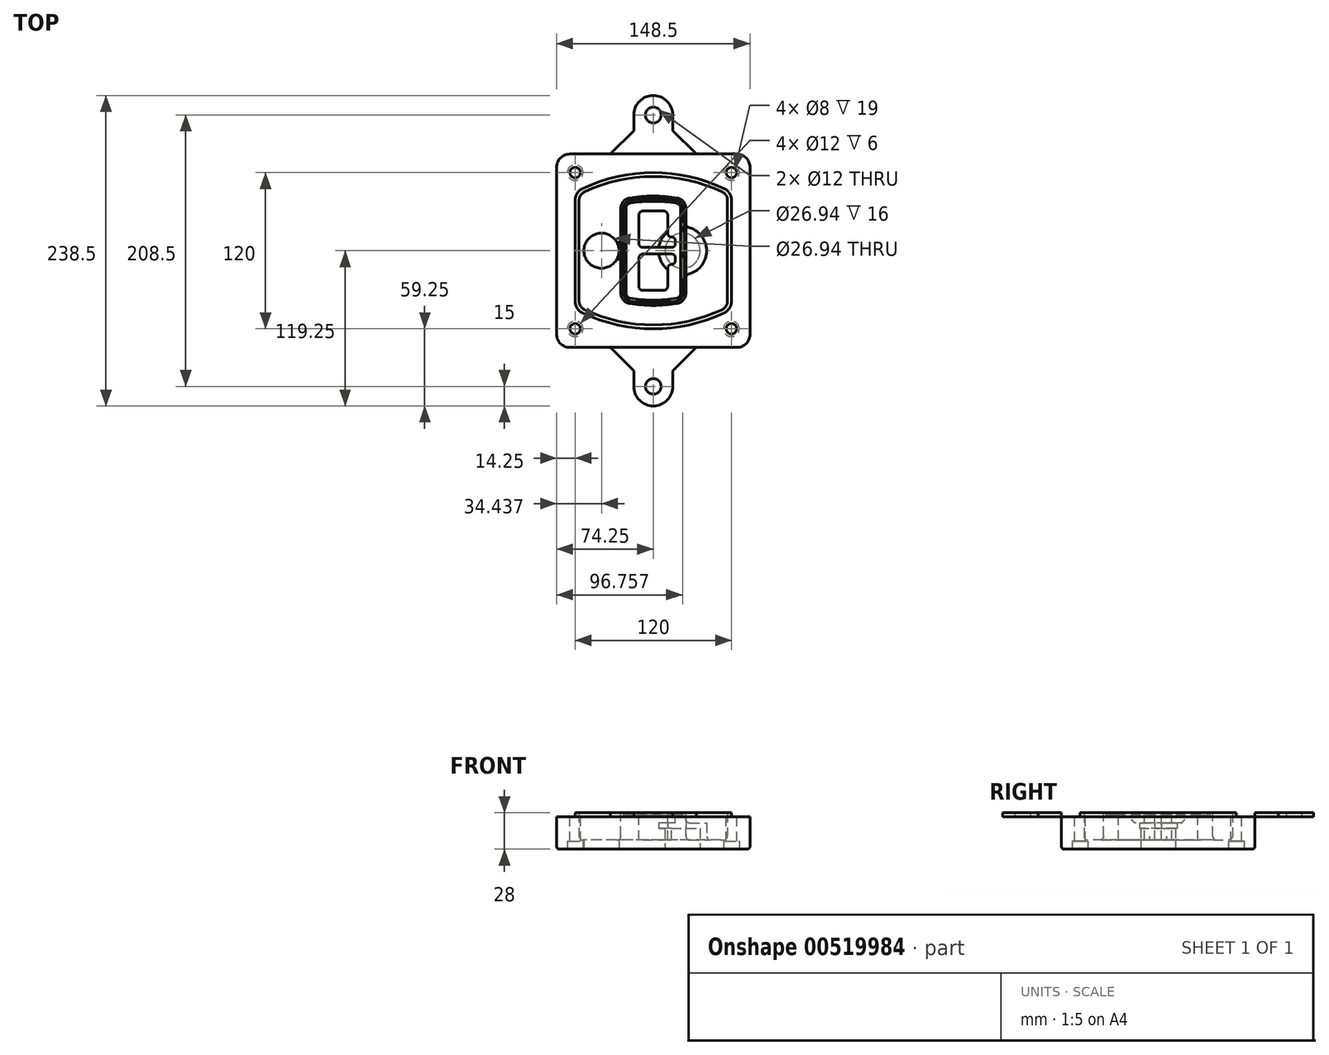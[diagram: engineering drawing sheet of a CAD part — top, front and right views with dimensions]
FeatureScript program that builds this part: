
annotation { "Feature Type Name" : "Feature", "Feature Type Description" : "" }
export const myFeature = defineFeature(function(context is Context, id is Id, definition is map)
    precondition{}
    {
        {
            var Q0;
            Q0=qCreatedBy(makeId("Top.planeOp"),FACE);
            var sketch = newSketch(context, id + "F0", { "sketchPlane" : qUnion([Q0])});
            skPoint(sketch, "E0.rect.middle", {"position": v(0, 0) * mm});
            skLineSegment(sketch, "E1.bottom", {"start": v(-64.25, -74.25) * mm, "end": v(64.25, -74.25) * mm});
            skLineSegment(sketch, "E1.top", {"start": v(-64.25, 74.25) * mm, "end": v(64.25, 74.25) * mm});
            skLineSegment(sketch, "E1.left", {"start": v(-74.25, -64.25) * mm, "end": v(-74.25, 64.25) * mm});
            skLineSegment(sketch, "E1.right", {"start": v(74.25, -64.25) * mm, "end": v(74.25, 64.25) * mm});
            skLineSegment(sketch, "E2", {"start": v(-74.25, 74.25) * mm, "end": v(74.25, -74.25) * mm, "construction": true});
            skLineSegment(sketch, "E3", {"start": v(74.25, 74.25) * mm, "end": v(-74.25, -74.25) * mm, "construction": true});
            skCircle(sketch, "E4", {"center": v(-60, 60) * mm, "radius": 4 * mm});
            skCircle(sketch, "E5", {"center": v(60, 60) * mm, "radius": 4 * mm});
            skCircle(sketch, "E6", {"center": v(60, -60) * mm, "radius": 4 * mm});
            skCircle(sketch, "E7", {"center": v(-60, -60) * mm, "radius": 4 * mm});
            skLineSegment(sketch, "E8", {"start": v(-60, 60) * mm, "end": v(60, 60) * mm, "construction": true});
            skLineSegment(sketch, "E9", {"start": v(60, 60) * mm, "end": v(60, -60) * mm, "construction": true});
            skLineSegment(sketch, "E10", {"start": v(60, -60) * mm, "end": v(-60, -60) * mm, "construction": true});
            skLineSegment(sketch, "E11", {"start": v(-60, -60) * mm, "end": v(-60, 60) * mm, "construction": true});
            skLineSegment(sketch, "E12", {"start": v(-60, 38.83) * mm, "end": v(-60, -38.83) * mm});
            skLineSegment(sketch, "E13", {"start": v(60, 38.83) * mm, "end": v(60, -38.83) * mm});
            skArc(sketch, "E14", {"start": v(54.26, 47.88) * mm, "mid": v(0, 60) * mm, "end": v(-54.26, 47.88) * mm});
            skArc(sketch, "E15", {"start": v(-54.26, -47.88) * mm, "mid": v(0, -60) * mm, "end": v(54.26, -47.88) * mm});
            skLineSegment(sketch, "E16", {"start": v(-60, 0) * mm, "end": v(60, 0) * mm, "construction": true});
            skPoint(sketch, "E17.visualSharp", {"position": v(-60, -45) * mm});
            skArc(sketch, "E17.filletArc", {"start": v(-60, -38.83) * mm, "mid": v(-58.44, -44.2) * mm, "end": v(-54.26, -47.88) * mm});
            skPoint(sketch, "E18.visualSharp", {"position": v(-60, 45) * mm});
            skArc(sketch, "E18.filletArc", {"start": v(-54.26, 47.88) * mm, "mid": v(-58.44, 44.2) * mm, "end": v(-60, 38.83) * mm});
            skPoint(sketch, "E19.visualSharp", {"position": v(60, 45) * mm});
            skArc(sketch, "E19.filletArc", {"start": v(60, 38.83) * mm, "mid": v(58.44, 44.2) * mm, "end": v(54.26, 47.88) * mm});
            skPoint(sketch, "E20.visualSharp", {"position": v(60, -45) * mm});
            skArc(sketch, "E20.filletArc", {"start": v(54.26, -47.88) * mm, "mid": v(58.44, -44.2) * mm, "end": v(60, -38.83) * mm});
            skPoint(sketch, "E21.visualSharp", {"position": v(-74.25, 74.25) * mm});
            skArc(sketch, "E21.filletArc", {"start": v(-64.25, 74.25) * mm, "mid": v(-71.32, 71.32) * mm, "end": v(-74.25, 64.25) * mm});
            skPoint(sketch, "E22.visualSharp", {"position": v(74.25, 74.25) * mm});
            skArc(sketch, "E22.filletArc", {"start": v(74.25, 64.25) * mm, "mid": v(71.32, 71.32) * mm, "end": v(64.25, 74.25) * mm});
            skPoint(sketch, "E23.visualSharp", {"position": v(74.25, -74.25) * mm});
            skArc(sketch, "E23.filletArc", {"start": v(64.25, -74.25) * mm, "mid": v(71.32, -71.32) * mm, "end": v(74.25, -64.25) * mm});
            skPoint(sketch, "E24.visualSharp", {"position": v(-74.25, -74.25) * mm});
            skArc(sketch, "E24.filletArc", {"start": v(-74.25, -64.25) * mm, "mid": v(-71.32, -71.32) * mm, "end": v(-64.25, -74.25) * mm});
            skArc(sketch, "E25.0", {"start": v(57, 38.83) * mm, "mid": v(55.9, 42.58) * mm, "end": v(52.98, 45.17) * mm});
            skLineSegment(sketch, "E25.1", {"start": v(57, 38.83) * mm, "end": v(57, -38.83) * mm});
            skArc(sketch, "E25.2", {"start": v(52.98, -45.17) * mm, "mid": v(55.9, -42.58) * mm, "end": v(57, -38.83) * mm});
            skArc(sketch, "E25.3", {"start": v(-52.98, -45.17) * mm, "mid": v(0, -57) * mm, "end": v(52.98, -45.17) * mm});
            skArc(sketch, "E25.4", {"start": v(-57, -38.83) * mm, "mid": v(-55.9, -42.58) * mm, "end": v(-52.98, -45.17) * mm});
            skArc(sketch, "E25.5", {"start": v(52.98, 45.17) * mm, "mid": v(0, 57) * mm, "end": v(-52.98, 45.17) * mm});
            skLineSegment(sketch, "E25.6", {"start": v(-57, 38.83) * mm, "end": v(-57, -38.83) * mm});
            skArc(sketch, "E25.7", {"start": v(-52.98, 45.17) * mm, "mid": v(-55.9, 42.58) * mm, "end": v(-57, 38.83) * mm});
            skArc(sketch, "E26.0", {"start": v(-55.96, 51.5) * mm, "mid": v(-61.82, 46.33) * mm, "end": v(-64, 38.83) * mm});
            skArc(sketch, "E26.1", {"start": v(55.96, 51.5) * mm, "mid": v(0, 64) * mm, "end": v(-55.96, 51.5) * mm});
            skArc(sketch, "E26.2", {"start": v(64, 38.83) * mm, "mid": v(61.82, 46.33) * mm, "end": v(55.96, 51.5) * mm});
            skLineSegment(sketch, "E26.3", {"start": v(64, 38.83) * mm, "end": v(64, -38.83) * mm});
            skArc(sketch, "E26.4", {"start": v(55.96, -51.5) * mm, "mid": v(61.82, -46.33) * mm, "end": v(64, -38.83) * mm});
            skLineSegment(sketch, "E26.5", {"start": v(-64, 38.83) * mm, "end": v(-64, -38.83) * mm});
            skArc(sketch, "E26.6", {"start": v(-55.96, -51.5) * mm, "mid": v(0, -64) * mm, "end": v(55.96, -51.5) * mm});
            skArc(sketch, "E26.7", {"start": v(-64, -38.83) * mm, "mid": v(-61.82, -46.33) * mm, "end": v(-55.96, -51.5) * mm});
            skSolve(sketch);
        }
        {
            var Q0;
            Q0=makeQuery(id+"F0.imprint","IMPRINT",FACE,{"disambiguationData":[TD([[makeQuery(id+"F0.imprint","IMPRINT",EDGE,{"derivedFrom":sQuery(id+"F0.wireOp",EDGE,"E1.bottom")}),1.0]])]});
            var Q1;
            Q1=makeQuery(id+"F0.imprint","IMPRINT",FACE,{"disambiguationData":[TD([[makeQuery(id+"F0.imprint","IMPRINT",EDGE,{"derivedFrom":sQuery(id+"F0.wireOp",EDGE,"E12")}),1.0]])]});
            var Q2;
            Q2=makeQuery(id+"F0.imprint","IMPRINT",FACE,{"disambiguationData":[TD([[makeQuery(id+"F0.imprint","IMPRINT",EDGE,{"derivedFrom":sQuery(id+"F0.wireOp",EDGE,"E25.0")}),1.0]])]});
            var Q3;
            Q3=makeQuery(id+"F0.imprint","IMPRINT",FACE,{"disambiguationData":[TD([[makeQuery(id+"F0.imprint","IMPRINT",EDGE,{"derivedFrom":sQuery(id+"F0.wireOp",EDGE,"E12")}),-1.0]])]});
            extrude(context, id + "F1", {"entities" : qUnion([Q0, Q1, Q2, Q3]), "oppositeDirection" : true, "depth" : 25 * mm});
        }
        {
            var Q0;
            Q0=makeQuery(id+"F0.imprint","IMPRINT",FACE,{"disambiguationData":[TD([[makeQuery(id+"F0.imprint","IMPRINT",EDGE,{"derivedFrom":sQuery(id+"F0.wireOp",EDGE,"E12")}),1.0]])]});
            extrude(context, id + "F2", {"entities" : qUnion([Q0]), "operationType" : NewBodyOperationType.ADD, "depth" : 3 * mm});
        }
        {
            var Q0;
            Q0=makeQuery(id+"F0.imprint","IMPRINT",FACE,{"disambiguationData":[TD([[makeQuery(id+"F0.imprint","IMPRINT",EDGE,{"derivedFrom":sQuery(id+"F0.wireOp",EDGE,"E25.0")}),1.0]])]});
            extrude(context, id + "F3", {"entities" : qUnion([Q0]), "operationType" : NewBodyOperationType.REMOVE, "oppositeDirection" : true, "depth" : 18 * mm});
        }
        {
            var Q0;
            Q0=makeQuery(id+"F2.opExtrude","CAP_FACE",FACE,{"disambiguationData":[OSD([sQuery(id+"F0.wireOp",EDGE,"E12"),sQuery(id+"F0.wireOp",EDGE,"E13"),sQuery(id+"F0.wireOp",EDGE,"E14"),sQuery(id+"F0.wireOp",EDGE,"E15"),sQuery(id+"F0.wireOp",EDGE,"E17.filletArc"),sQuery(id+"F0.wireOp",EDGE,"E18.filletArc"),sQuery(id+"F0.wireOp",EDGE,"E19.filletArc"),sQuery(id+"F0.wireOp",EDGE,"E20.filletArc"),sQuery(id+"F0.wireOp",EDGE,"E25.0"),sQuery(id+"F0.wireOp",EDGE,"E25.1"),sQuery(id+"F0.wireOp",EDGE,"E25.2"),sQuery(id+"F0.wireOp",EDGE,"E25.3"),sQuery(id+"F0.wireOp",EDGE,"E25.4"),sQuery(id+"F0.wireOp",EDGE,"E25.5"),sQuery(id+"F0.wireOp",EDGE,"E25.6"),sQuery(id+"F0.wireOp",EDGE,"E25.7")])],"isStart":false});
            var sketch = newSketch(context, id + "F4", { "sketchPlane" : qUnion([Q0])});
            skArc(sketch, "E27.0", {"start": v(-18.34, -40.45) * mm, "mid": v(0, -42) * mm, "end": v(18.34, -40.45) * mm});
            skArc(sketch, "E28.0", {"start": v(18.34, 40.45) * mm, "mid": v(0, 42) * mm, "end": v(-18.34, 40.45) * mm});
            skLineSegment(sketch, "E29", {"start": v(-25, 32.57) * mm, "end": v(-25, -32.57) * mm});
            skLineSegment(sketch, "E30", {"start": v(25, 32.57) * mm, "end": v(25, -32.57) * mm});
            skLineSegment(sketch, "E31", {"start": v(-25, 39.1) * mm, "end": v(25, 39.1) * mm, "construction": true});
            skLineSegment(sketch, "E32", {"start": v(-25, -39.1) * mm, "end": v(25, -39.1) * mm, "construction": true});
            skPoint(sketch, "E33.visualSharp", {"position": v(-25, 39.1) * mm});
            skArc(sketch, "E33.filletArc", {"start": v(-18.34, 40.45) * mm, "mid": v(-23.11, 37.73) * mm, "end": v(-25, 32.57) * mm});
            skPoint(sketch, "E34.visualSharp", {"position": v(25, 39.1) * mm});
            skArc(sketch, "E34.filletArc", {"start": v(25, 32.57) * mm, "mid": v(23.11, 37.73) * mm, "end": v(18.34, 40.45) * mm});
            skPoint(sketch, "E35.visualSharp", {"position": v(25, -39.1) * mm});
            skArc(sketch, "E35.filletArc", {"start": v(18.34, -40.45) * mm, "mid": v(23.11, -37.73) * mm, "end": v(25, -32.57) * mm});
            skPoint(sketch, "E36.visualSharp", {"position": v(-25, -39.1) * mm});
            skArc(sketch, "E36.filletArc", {"start": v(-25, -32.57) * mm, "mid": v(-23.11, -37.73) * mm, "end": v(-18.34, -40.45) * mm});
            skArc(sketch, "E37.0", {"start": v(52.98, 45.17) * mm, "mid": v(0, 57) * mm, "end": v(-52.98, 45.17) * mm});
            skArc(sketch, "E37.1", {"start": v(-52.98, 45.17) * mm, "mid": v(-55.9, 42.58) * mm, "end": v(-57, 38.83) * mm});
            skLineSegment(sketch, "E37.2", {"start": v(-57, 38.83) * mm, "end": v(-57, -38.83) * mm});
            skArc(sketch, "E37.3", {"start": v(-57, -38.83) * mm, "mid": v(-55.9, -42.58) * mm, "end": v(-52.98, -45.17) * mm});
            skArc(sketch, "E37.4", {"start": v(-52.98, -45.17) * mm, "mid": v(0, -57) * mm, "end": v(52.98, -45.17) * mm});
            skArc(sketch, "E37.5", {"start": v(52.98, -45.17) * mm, "mid": v(55.9, -42.58) * mm, "end": v(57, -38.83) * mm});
            skLineSegment(sketch, "E37.6", {"start": v(57, 38.83) * mm, "end": v(57, -38.83) * mm});
            skArc(sketch, "E37.7", {"start": v(57, 38.83) * mm, "mid": v(55.9, 42.58) * mm, "end": v(52.98, 45.17) * mm});
            skLineSegment(sketch, "E38.0", {"start": v(23, 32.57) * mm, "end": v(23, -32.57) * mm});
            skArc(sketch, "E38.1", {"start": v(18, -38.48) * mm, "mid": v(21.58, -36.44) * mm, "end": v(23, -32.57) * mm});
            skArc(sketch, "E38.2", {"start": v(-18, -38.48) * mm, "mid": v(0, -40) * mm, "end": v(18, -38.48) * mm});
            skArc(sketch, "E38.3", {"start": v(-23, -32.57) * mm, "mid": v(-21.58, -36.44) * mm, "end": v(-18, -38.48) * mm});
            skLineSegment(sketch, "E38.4", {"start": v(-23, 32.57) * mm, "end": v(-23, -32.57) * mm});
            skArc(sketch, "E38.5", {"start": v(23, 32.57) * mm, "mid": v(21.58, 36.44) * mm, "end": v(18, 38.48) * mm});
            skArc(sketch, "E38.6", {"start": v(-18, 38.48) * mm, "mid": v(-21.58, 36.44) * mm, "end": v(-23, 32.57) * mm});
            skArc(sketch, "E38.7", {"start": v(18, 38.48) * mm, "mid": v(0, 40) * mm, "end": v(-18, 38.48) * mm});
            skArc(sketch, "E39.0", {"start": v(21, 32.57) * mm, "mid": v(20.06, 35.15) * mm, "end": v(17.67, 36.5) * mm});
            skLineSegment(sketch, "E39.1", {"start": v(21, 32.57) * mm, "end": v(21, -32.57) * mm});
            skArc(sketch, "E39.2", {"start": v(17.67, -36.5) * mm, "mid": v(20.06, -35.15) * mm, "end": v(21, -32.57) * mm});
            skArc(sketch, "E39.3", {"start": v(-17.67, -36.5) * mm, "mid": v(0, -38) * mm, "end": v(17.67, -36.5) * mm});
            skArc(sketch, "E39.4", {"start": v(-21, -32.57) * mm, "mid": v(-20.06, -35.15) * mm, "end": v(-17.67, -36.5) * mm});
            skArc(sketch, "E39.5", {"start": v(17.67, 36.5) * mm, "mid": v(0, 38) * mm, "end": v(-17.67, 36.5) * mm});
            skLineSegment(sketch, "E39.6", {"start": v(-21, 32.57) * mm, "end": v(-21, -32.57) * mm});
            skArc(sketch, "E39.7", {"start": v(-17.67, 36.5) * mm, "mid": v(-20.06, 35.15) * mm, "end": v(-21, 32.57) * mm});
            skLineSegment(sketch, "E40", {"start": v(-25, 0) * mm, "end": v(25, 0) * mm, "construction": true});
            skLineSegment(sketch, "E41", {"start": v(-11, 5.5) * mm, "end": v(-11, 27.5) * mm});
            skLineSegment(sketch, "E42", {"start": v(-8, 30.5) * mm, "end": v(8, 30.5) * mm});
            skLineSegment(sketch, "E43", {"start": v(11, 27.5) * mm, "end": v(11, 13.5) * mm});
            skLineSegment(sketch, "E44", {"start": v(14, 10.5) * mm, "end": v(14, 10.5) * mm});
            skLineSegment(sketch, "E45", {"start": v(17, 7.5) * mm, "end": v(17, 5.5) * mm});
            skLineSegment(sketch, "E46", {"start": v(14, 2.5) * mm, "end": v(-8, 2.5) * mm});
            skPoint(sketch, "E47.visualSharp", {"position": v(-11, 30.5) * mm});
            skArc(sketch, "E47.filletArc", {"start": v(-8, 30.5) * mm, "mid": v(-10.12, 29.62) * mm, "end": v(-11, 27.5) * mm});
            skPoint(sketch, "E48.visualSharp", {"position": v(11, 30.5) * mm});
            skArc(sketch, "E48.filletArc", {"start": v(11, 27.5) * mm, "mid": v(10.12, 29.62) * mm, "end": v(8, 30.5) * mm});
            skPoint(sketch, "E49.visualSharp", {"position": v(11, 10.5) * mm});
            skArc(sketch, "E49.filletArc", {"start": v(11, 13.5) * mm, "mid": v(11.88, 11.38) * mm, "end": v(14, 10.5) * mm});
            skPoint(sketch, "E50.visualSharp", {"position": v(17, 10.5) * mm});
            skArc(sketch, "E50.filletArc", {"start": v(17, 7.5) * mm, "mid": v(16.12, 9.62) * mm, "end": v(14, 10.5) * mm});
            skPoint(sketch, "E51.visualSharp", {"position": v(17, 2.5) * mm});
            skArc(sketch, "E51.filletArc", {"start": v(14, 2.5) * mm, "mid": v(16.12, 3.38) * mm, "end": v(17, 5.5) * mm});
            skPoint(sketch, "E52.visualSharp", {"position": v(-11, 2.5) * mm});
            skArc(sketch, "E52.filletArc", {"start": v(-11, 5.5) * mm, "mid": v(-10.12, 3.38) * mm, "end": v(-8, 2.5) * mm});
            skLineSegment(sketch, "E53.0.MirrorCS", {"start": v(14, -2.5) * mm, "end": v(-8, -2.5) * mm});
            skArc(sketch, "E54.0.MirrorCS", {"start": v(-11, -5.5) * mm, "mid": v(-10.12, -3.38) * mm, "end": v(-8, -2.5) * mm});
            skLineSegment(sketch, "E55.0.MirrorCS", {"start": v(-11, -5.5) * mm, "end": v(-11, -27.5) * mm});
            skArc(sketch, "E56.0.MirrorCS", {"start": v(-8, -30.5) * mm, "mid": v(-10.12, -29.62) * mm, "end": v(-11, -27.5) * mm});
            skLineSegment(sketch, "E57.0.MirrorCS", {"start": v(-8, -30.5) * mm, "end": v(8, -30.5) * mm});
            skArc(sketch, "E58.0.MirrorCS", {"start": v(11, -27.5) * mm, "mid": v(10.12, -29.62) * mm, "end": v(8, -30.5) * mm});
            skLineSegment(sketch, "E59.0.MirrorCS", {"start": v(11, -27.5) * mm, "end": v(11, -13.5) * mm});
            skArc(sketch, "E60.0.MirrorCS", {"start": v(11, -13.5) * mm, "mid": v(11.88, -11.38) * mm, "end": v(14, -10.5) * mm});
            skArc(sketch, "E61.0.MirrorCS", {"start": v(17, -7.5) * mm, "mid": v(16.12, -9.62) * mm, "end": v(14, -10.5) * mm});
            skLineSegment(sketch, "E62.0.MirrorCS", {"start": v(17, -7.5) * mm, "end": v(17, -5.5) * mm});
            skArc(sketch, "E63.0.MirrorCS", {"start": v(14, -2.5) * mm, "mid": v(16.12, -3.38) * mm, "end": v(17, -5.5) * mm});
            skSolve(sketch);
        }
        {
            var Q0;
            Q0=makeQuery(id+"F4.imprint","IMPRINT",FACE,{"disambiguationData":[TD([[makeQuery(id+"F4.imprint","IMPRINT",EDGE,{"derivedFrom":sQuery(id+"F4.wireOp",EDGE,"E27.0")}),1.0]])]});
            var Q1;
            Q1=makeQuery(id+"F4.imprint","IMPRINT",FACE,{"disambiguationData":[TD([[makeQuery(id+"F4.imprint","IMPRINT",EDGE,{"derivedFrom":sQuery(id+"F4.wireOp",EDGE,"E38.0")}),-1.0]])]});
            var Q2;
            Q2=makeQuery(id+"F4.imprint","IMPRINT",FACE,{"disambiguationData":[TD([[makeQuery(id+"F4.imprint","IMPRINT",EDGE,{"derivedFrom":sQuery(id+"F4.wireOp",EDGE,"E39.0")}),1.0]])]});
            extrude(context, id + "F5", {"entities" : qUnion([Q0, Q1, Q2]), "operationType" : NewBodyOperationType.ADD, "endBound" : BoundingType.UP_TO_NEXT, "oppositeDirection" : true, "depth" : 25 * mm});
        }
        {
            var Q0;
            Q0=makeQuery(id+"F4.imprint","IMPRINT",FACE,{"disambiguationData":[TD([[makeQuery(id+"F4.imprint","IMPRINT",EDGE,{"derivedFrom":sQuery(id+"F4.wireOp",EDGE,"E38.0")}),-1.0]])]});
            extrude(context, id + "F6", {"entities" : qUnion([Q0]), "operationType" : NewBodyOperationType.REMOVE, "oppositeDirection" : true, "depth" : 2 * mm});
        }
        {
            var Q0;
            Q0=makeQuery(id+"F1.opExtrude","CAP_FACE",FACE,{"disambiguationData":[OSD([sQuery(id+"F0.wireOp",EDGE,"E1.bottom"),sQuery(id+"F0.wireOp",EDGE,"E1.top"),sQuery(id+"F0.wireOp",EDGE,"E1.left"),sQuery(id+"F0.wireOp",EDGE,"E1.right"),sQuery(id+"F0.wireOp",EDGE,"E4"),sQuery(id+"F0.wireOp",EDGE,"E5"),sQuery(id+"F0.wireOp",EDGE,"E6"),sQuery(id+"F0.wireOp",EDGE,"E7"),sQuery(id+"F0.wireOp",EDGE,"E21.filletArc"),sQuery(id+"F0.wireOp",EDGE,"E22.filletArc"),sQuery(id+"F0.wireOp",EDGE,"E23.filletArc"),sQuery(id+"F0.wireOp",EDGE,"E24.filletArc")])],"isStart":false});
            var sketch = newSketch(context, id + "F7", { "sketchPlane" : qUnion([Q0])});
            skCircle(sketch, "E64", {"center": v(22.5, 0) * mm, "radius": 13.47 * mm});
            skCircle(sketch, "E65", {"center": v(-39.81, 0) * mm, "radius": 13.47 * mm});
            skLineSegment(sketch, "E66", {"start": v(74.25, 0) * mm, "end": v(-74.25, 0) * mm});
            skCircle(sketch, "E67", {"center": v(22.5, 0) * mm, "radius": 18.47 * mm});
            skCircle(sketch, "E68", {"center": v(60, -60) * mm, "radius": 6 * mm});
            skCircle(sketch, "E69", {"center": v(-60, -60) * mm, "radius": 6 * mm});
            skCircle(sketch, "E70", {"center": v(-60, 60) * mm, "radius": 6 * mm});
            skCircle(sketch, "E71", {"center": v(60, 60) * mm, "radius": 6 * mm});
            skSolve(sketch);
        }
        {
            var Q0;
            {var subQ1=sQuery(id+"F7.wireOp",EDGE,"E66");var subQ4=sQuery(id+"F7.wireOp",EDGE,"E64");var subQ6=makeQuery(id+"F7.imprint","INTERSECT",VERTEX,{"disambiguationData":[OD(0.0)],"derivedFrom":[subQ4,subQ1]});Q0=makeQuery(id+"F7.imprint","IMPRINT",FACE,{"disambiguationData":[TD([[makeQuery(id+"F7.imprint","IMPRINT",EDGE,{"disambiguationData":[TD([[subQ6,-1.0]])],"derivedFrom":subQ4}),-1.0]])]});}
            var Q1;
            {var subQ0=sQuery(id+"F7.wireOp",EDGE,"E66");var subQ1=sQuery(id+"F7.wireOp",EDGE,"E64");var subQ3=makeQuery(id+"F7.imprint","INTERSECT",VERTEX,{"disambiguationData":[OD(0.0)],"derivedFrom":[subQ1,subQ0]});Q1=makeQuery(id+"F7.imprint","IMPRINT",FACE,{"disambiguationData":[TD([[makeQuery(id+"F7.imprint","IMPRINT",EDGE,{"disambiguationData":[TD([[subQ3,-1.0]])],"derivedFrom":subQ1}),1.0]])]});}
            var Q2;
            {var subQ0=sQuery(id+"F7.wireOp",EDGE,"E66");var subQ1=sQuery(id+"F7.wireOp",EDGE,"E64");var subQ3=makeQuery(id+"F7.imprint","INTERSECT",VERTEX,{"disambiguationData":[OD(0.0)],"derivedFrom":[subQ1,subQ0]});Q2=makeQuery(id+"F7.imprint","IMPRINT",FACE,{"disambiguationData":[TD([[makeQuery(id+"F7.imprint","IMPRINT",EDGE,{"disambiguationData":[TD([[subQ3,1.0]])],"derivedFrom":subQ1}),1.0]])]});}
            var Q3;
            {var subQ1=sQuery(id+"F7.wireOp",EDGE,"E66");var subQ4=sQuery(id+"F7.wireOp",EDGE,"E64");var subQ6=makeQuery(id+"F7.imprint","INTERSECT",VERTEX,{"disambiguationData":[OD(0.0)],"derivedFrom":[subQ4,subQ1]});Q3=makeQuery(id+"F7.imprint","IMPRINT",FACE,{"disambiguationData":[TD([[makeQuery(id+"F7.imprint","IMPRINT",EDGE,{"disambiguationData":[TD([[subQ6,1.0]])],"derivedFrom":subQ4}),-1.0]])]});}
            extrude(context, id + "F8", {"entities" : qUnion([Q0, Q1, Q2, Q3]), "operationType" : NewBodyOperationType.ADD, "oppositeDirection" : true, "depth" : 20 * mm});
        }
        {
            var Q0;
            {var subQ0=sQuery(id+"F7.wireOp",EDGE,"E66");var subQ1=sQuery(id+"F7.wireOp",EDGE,"E64");var subQ3=makeQuery(id+"F7.imprint","INTERSECT",VERTEX,{"disambiguationData":[OD(0.0)],"derivedFrom":[subQ1,subQ0]});Q0=makeQuery(id+"F7.imprint","IMPRINT",FACE,{"disambiguationData":[TD([[makeQuery(id+"F7.imprint","IMPRINT",EDGE,{"disambiguationData":[TD([[subQ3,-1.0]])],"derivedFrom":subQ1}),1.0]])]});}
            var Q1;
            {var subQ0=sQuery(id+"F7.wireOp",EDGE,"E66");var subQ1=sQuery(id+"F7.wireOp",EDGE,"E64");var subQ3=makeQuery(id+"F7.imprint","INTERSECT",VERTEX,{"disambiguationData":[OD(0.0)],"derivedFrom":[subQ1,subQ0]});Q1=makeQuery(id+"F7.imprint","IMPRINT",FACE,{"disambiguationData":[TD([[makeQuery(id+"F7.imprint","IMPRINT",EDGE,{"disambiguationData":[TD([[subQ3,1.0]])],"derivedFrom":subQ1}),1.0]])]});}
            extrude(context, id + "F9", {"entities" : qUnion([Q0, Q1]), "operationType" : NewBodyOperationType.REMOVE, "oppositeDirection" : true, "depth" : 16 * mm});
        }
        {
            var Q0;
            {var subQ0=sQuery(id+"F7.wireOp",EDGE,"E66");var subQ1=sQuery(id+"F7.wireOp",EDGE,"E65");var subQ3=makeQuery(id+"F7.imprint","INTERSECT",VERTEX,{"disambiguationData":[OD(0.0)],"derivedFrom":[subQ1,subQ0]});Q0=makeQuery(id+"F7.imprint","IMPRINT",FACE,{"disambiguationData":[TD([[makeQuery(id+"F7.imprint","IMPRINT",EDGE,{"disambiguationData":[TD([[subQ3,-1.0]])],"derivedFrom":subQ1}),1.0]])]});}
            var Q1;
            {var subQ0=sQuery(id+"F7.wireOp",EDGE,"E66");var subQ1=sQuery(id+"F7.wireOp",EDGE,"E65");var subQ3=makeQuery(id+"F7.imprint","INTERSECT",VERTEX,{"disambiguationData":[OD(0.0)],"derivedFrom":[subQ1,subQ0]});Q1=makeQuery(id+"F7.imprint","IMPRINT",FACE,{"disambiguationData":[TD([[makeQuery(id+"F7.imprint","IMPRINT",EDGE,{"disambiguationData":[TD([[subQ3,1.0]])],"derivedFrom":subQ1}),1.0]])]});}
            extrude(context, id + "F10", {"entities" : qUnion([Q0, Q1]), "operationType" : NewBodyOperationType.REMOVE, "oppositeDirection" : true, "depth" : 25 * mm});
        }
        {
            var Q0;
            Q0=makeQuery(id+"F7.imprint","IMPRINT",FACE,{"disambiguationData":[TD([[makeQuery(id+"F7.imprint","IMPRINT",EDGE,{"derivedFrom":sQuery(id+"F7.wireOp",EDGE,"E68")}),1.0]])]});
            var Q1;
            Q1=makeQuery(id+"F7.imprint","IMPRINT",FACE,{"disambiguationData":[TD([[makeQuery(id+"F7.imprint","IMPRINT",EDGE,{"derivedFrom":makeQuery(id+"F1.opExtrude","CAP_EDGE",EDGE,{"disambiguationData":[OSD([sQuery(id+"F0.wireOp",EDGE,"E5")])],"isStart":false})}),-1.0]])]});
            var Q2;
            Q2=makeQuery(id+"F7.imprint","IMPRINT",FACE,{"disambiguationData":[TD([[makeQuery(id+"F7.imprint","IMPRINT",EDGE,{"derivedFrom":sQuery(id+"F7.wireOp",EDGE,"E69")}),1.0]])]});
            var Q3;
            Q3=makeQuery(id+"F7.imprint","IMPRINT",FACE,{"disambiguationData":[TD([[makeQuery(id+"F7.imprint","IMPRINT",EDGE,{"derivedFrom":makeQuery(id+"F1.opExtrude","CAP_EDGE",EDGE,{"disambiguationData":[OSD([sQuery(id+"F0.wireOp",EDGE,"E4")])],"isStart":false})}),-1.0]])]});
            var Q4;
            Q4=makeQuery(id+"F7.imprint","IMPRINT",FACE,{"disambiguationData":[TD([[makeQuery(id+"F7.imprint","IMPRINT",EDGE,{"derivedFrom":sQuery(id+"F7.wireOp",EDGE,"E70")}),1.0]])]});
            var Q5;
            Q5=makeQuery(id+"F7.imprint","IMPRINT",FACE,{"disambiguationData":[TD([[makeQuery(id+"F7.imprint","IMPRINT",EDGE,{"derivedFrom":makeQuery(id+"F1.opExtrude","CAP_EDGE",EDGE,{"disambiguationData":[OSD([sQuery(id+"F0.wireOp",EDGE,"E7")])],"isStart":false})}),-1.0]])]});
            var Q6;
            Q6=makeQuery(id+"F7.imprint","IMPRINT",FACE,{"disambiguationData":[TD([[makeQuery(id+"F7.imprint","IMPRINT",EDGE,{"derivedFrom":sQuery(id+"F7.wireOp",EDGE,"E71")}),1.0]])]});
            var Q7;
            Q7=makeQuery(id+"F7.imprint","IMPRINT",FACE,{"disambiguationData":[TD([[makeQuery(id+"F7.imprint","IMPRINT",EDGE,{"derivedFrom":makeQuery(id+"F1.opExtrude","CAP_EDGE",EDGE,{"disambiguationData":[OSD([sQuery(id+"F0.wireOp",EDGE,"E6")])],"isStart":false})}),-1.0]])]});
            extrude(context, id + "F11", {"entities" : qUnion([Q0, Q1, Q2, Q3, Q4, Q5, Q6, Q7]), "operationType" : NewBodyOperationType.REMOVE, "oppositeDirection" : true, "depth" : 6 * mm});
        }
        {
            var Q0;
            Q0=makeQuery(id+"F9.boolean.opBoolean","COPY",FACE,{"derivedFrom":makeQuery(id+"F9.opExtrude","CAP_FACE",FACE,{"disambiguationData":[OSD([sQuery(id+"F7.wireOp",EDGE,"E64")])],"isStart":false})});
            var sketch = newSketch(context, id + "F12", { "sketchPlane" : qUnion([Q0])});
            skArc(sketch, "E72.0", {"start": v(11, 14.45) * mm, "mid": v(6.45, 9.13) * mm, "end": v(4.2, 2.5) * mm});
            skArc(sketch, "E72.1", {"start": v(4.2, -2.5) * mm, "mid": v(6.45, -9.13) * mm, "end": v(11, -14.45) * mm});
            skLineSegment(sketch, "E73", {"start": v(4.2, -2.5) * mm, "end": v(14, -2.5) * mm});
            skLineSegment(sketch, "E74.0", {"start": v(14, 2.5) * mm, "end": v(4.2, 2.5) * mm});
            skArc(sketch, "E74.1", {"start": v(14, 2.5) * mm, "mid": v(16.12, 3.38) * mm, "end": v(17, 5.5) * mm});
            skLineSegment(sketch, "E74.2", {"start": v(17, 7.5) * mm, "end": v(17, 5.5) * mm});
            skArc(sketch, "E74.3", {"start": v(17, 7.5) * mm, "mid": v(16.12, 9.62) * mm, "end": v(14, 10.5) * mm});
            skArc(sketch, "E74.4", {"start": v(11, 13.5) * mm, "mid": v(11.88, 11.38) * mm, "end": v(14, 10.5) * mm});
            skLineSegment(sketch, "E74.5", {"start": v(11, 14.45) * mm, "end": v(11, 13.5) * mm});
            skLineSegment(sketch, "E74.7", {"start": v(14, -2.5) * mm, "end": v(4.2, -2.5) * mm});
            skArc(sketch, "E74.8", {"start": v(14, -2.5) * mm, "mid": v(16.12, -3.38) * mm, "end": v(17, -5.5) * mm});
            skLineSegment(sketch, "E74.9", {"start": v(17, -7.5) * mm, "end": v(17, -5.5) * mm});
            skArc(sketch, "E74.10", {"start": v(17, -7.5) * mm, "mid": v(16.12, -9.62) * mm, "end": v(14, -10.5) * mm});
            skArc(sketch, "E74.11", {"start": v(11, -13.5) * mm, "mid": v(11.88, -11.38) * mm, "end": v(14, -10.5) * mm});
            skLineSegment(sketch, "E74.12", {"start": v(11, -14.45) * mm, "end": v(11, -13.5) * mm});
            skPoint(sketch, "E75.orphan", {"position": v(11, -27.5) * mm});
            skPoint(sketch, "E76.orphan", {"position": v(-8, -2.5) * mm});
            skPoint(sketch, "E77.orphan", {"position": v(-8, 2.5) * mm});
            skPoint(sketch, "E78.orphan", {"position": v(11, 27.5) * mm});
            skSolve(sketch);
        }
        {
            var Q0;
            {var subQ7=sQuery(id+"F12.wireOp",EDGE,"E72.0");var subQ14=sQuery(id+"F12.wireOp",EDGE,"E72.1");var subQ16=sQuery(id+"F12.wireOp",EDGE,"E74.1");var subQ18=sQuery(id+"F12.wireOp",EDGE,"E74.8");Q0=qUnion([makeQuery(id+"F12.imprint","IMPRINT",FACE,{"disambiguationData":[TD([[makeQuery(id+"F12.imprint","IMPRINT",EDGE,{"derivedFrom":subQ7}),1.0]])]}),makeQuery(id+"F12.imprint","IMPRINT",FACE,{"disambiguationData":[TD([[makeQuery(id+"F12.imprint","IMPRINT",EDGE,{"derivedFrom":subQ14}),1.0]])]}),makeQuery(id+"F12.imprint","IMPRINT",FACE,{"disambiguationData":[TD([[makeQuery(id+"F12.imprint","IMPRINT",EDGE,{"derivedFrom":subQ16}),1.0]])]}),makeQuery(id+"F12.imprint","IMPRINT",FACE,{"disambiguationData":[TD([[makeQuery(id+"F12.imprint","IMPRINT",EDGE,{"derivedFrom":subQ18}),-1.0]])]})]);}
            var Q1;
            Q1=makeQuery(id+"F5.boolean.opBoolean","SPLIT",FACE,{"disambiguationData":[TD([makeQuery(id+"F5.opExtrude","SWEPT_FACE",FACE,{"disambiguationData":[OSD([sQuery(id+"F4.wireOp",EDGE,"E41")])]})])],"derivedFrom":makeQuery(id+"F3.boolean.opBoolean","COPY",FACE,{"derivedFrom":makeQuery(id+"F3.opExtrude","CAP_FACE",FACE,{"disambiguationData":[OSD([sQuery(id+"F0.wireOp",EDGE,"E25.0"),sQuery(id+"F0.wireOp",EDGE,"E25.1"),sQuery(id+"F0.wireOp",EDGE,"E25.2"),sQuery(id+"F0.wireOp",EDGE,"E25.3"),sQuery(id+"F0.wireOp",EDGE,"E25.4"),sQuery(id+"F0.wireOp",EDGE,"E25.5"),sQuery(id+"F0.wireOp",EDGE,"E25.6"),sQuery(id+"F0.wireOp",EDGE,"E25.7")])],"isStart":false})})});
            extrude(context, id + "F13", {"entities" : qUnion([Q0]), "operationType" : NewBodyOperationType.REMOVE, "endBound" : BoundingType.UP_TO_SURFACE, "endBoundEntityFace" : qUnion([Q1]), "depth" : 25 * mm});
        }
        {
            var Q0;
            Q0=makeQuery(id+"F3.boolean.opBoolean","COPY",EDGE,{"derivedFrom":makeQuery(id+"F3.opExtrude","CAP_EDGE",EDGE,{"disambiguationData":[OSD([sQuery(id+"F0.wireOp",EDGE,"E25.6")])],"isStart":false})});
            var Q1;
            Q1=makeQuery(id+"F8.boolean.opBoolean","INTERSECT",EDGE,{"derivedFrom":[makeQuery(id+"F5.opExtrude","SWEPT_FACE",FACE,{"disambiguationData":[OSD([sQuery(id+"F4.wireOp",EDGE,"E30")])]}),makeQuery(id+"F8.opExtrude","CAP_FACE",FACE,{"disambiguationData":[OSD([sQuery(id+"F7.wireOp",EDGE,"E67")])],"isStart":false})]});
            var Q2;
            Q2=makeQuery(id+"F8.boolean.opBoolean","INTERSECT",EDGE,{"disambiguationData":[OD(1.0)],"derivedFrom":[makeQuery(id+"F5.opExtrude","SWEPT_FACE",FACE,{"disambiguationData":[OSD([sQuery(id+"F4.wireOp",EDGE,"E30")])]}),makeQuery(id+"F8.opExtrude","SWEPT_FACE",FACE,{"disambiguationData":[OSD([sQuery(id+"F7.wireOp",EDGE,"E67")])]})]});
            var Q3;
            {var subQ0=sQuery(id+"F4.wireOp",EDGE,"E30");Q3=makeQuery(id+"F8.boolean.opBoolean","SPLIT",EDGE,{"disambiguationData":[TD([makeQuery(id+"F5.opExtrude","SWEPT_FACE",FACE,{"disambiguationData":[OSD([sQuery(id+"F4.wireOp",EDGE,"E35.filletArc")])]})])],"derivedFrom":makeQuery(id+"F5.opExtrude","CAP_EDGE",EDGE,{"disambiguationData":[OSD([subQ0])],"isStart":false})});}
            var Q4;
            {var subQ0=sQuery(id+"F0.wireOp",EDGE,"E25.7");var subQ1=sQuery(id+"F0.wireOp",EDGE,"E25.1");var subQ2=sQuery(id+"F0.wireOp",EDGE,"E25.6");var subQ3=sQuery(id+"F0.wireOp",EDGE,"E25.5");var subQ4=sQuery(id+"F0.wireOp",EDGE,"E25.4");var subQ5=sQuery(id+"F0.wireOp",EDGE,"E25.0");var subQ6=sQuery(id+"F0.wireOp",EDGE,"E25.2");var subQ7=sQuery(id+"F0.wireOp",EDGE,"E25.3");Q4=makeQuery(id+"F8.boolean.opBoolean","INTERSECT",EDGE,{"derivedFrom":[makeQuery(id+"F5.boolean.opBoolean","SPLIT",FACE,{"disambiguationData":[TD([makeQuery(id+"F2.opExtrude","SWEPT_FACE",FACE,{"disambiguationData":[OSD([subQ5])]})])],"derivedFrom":makeQuery(id+"F3.boolean.opBoolean","COPY",FACE,{"derivedFrom":makeQuery(id+"F3.opExtrude","CAP_FACE",FACE,{"disambiguationData":[OSD([subQ5,subQ1,subQ6,subQ7,subQ4,subQ3,subQ2,subQ0])],"isStart":false})})}),makeQuery(id+"F8.opExtrude","SWEPT_FACE",FACE,{"disambiguationData":[OSD([sQuery(id+"F7.wireOp",EDGE,"E67")])]})]});}
            var Q5;
            Q5=makeQuery(id+"F8.boolean.opBoolean","INTERSECT",EDGE,{"disambiguationData":[OD(0.0)],"derivedFrom":[makeQuery(id+"F5.opExtrude","SWEPT_FACE",FACE,{"disambiguationData":[OSD([sQuery(id+"F4.wireOp",EDGE,"E30")])]}),makeQuery(id+"F8.opExtrude","SWEPT_FACE",FACE,{"disambiguationData":[OSD([sQuery(id+"F7.wireOp",EDGE,"E67")])]})]});
            fillet(context, id + "F14", {"entities" : qUnion([Q0, Q1, Q2, Q3, Q4, Q5]), "radius" : 3 * mm, "tangentPropagation" : true, "allowEdgeOverflow" : false});
        }
        {
            var Q0;
            Q0=makeQuery(id+"F1.opExtrude","CAP_EDGE",EDGE,{"disambiguationData":[OSD([sQuery(id+"F0.wireOp",EDGE,"E1.bottom")])],"isStart":false});
            fillet(context, id + "F15", {"entities" : qUnion([Q0]), "radius" : 2 * mm, "tangentPropagation" : true, "allowEdgeOverflow" : false});
        }
        {
            var Q0;
            {var subQ0=sQuery(id+"F0.wireOp",EDGE,"E21.filletArc");var subQ1=sQuery(id+"F0.wireOp",EDGE,"E7");var subQ2=sQuery(id+"F0.wireOp",EDGE,"E6");var subQ3=sQuery(id+"F0.wireOp",EDGE,"E5");var subQ4=sQuery(id+"F0.wireOp",EDGE,"E4");var subQ5=sQuery(id+"F0.wireOp",EDGE,"E22.filletArc");var subQ6=sQuery(id+"F0.wireOp",EDGE,"E1.bottom");var subQ7=sQuery(id+"F0.wireOp",EDGE,"E1.right");var subQ8=sQuery(id+"F0.wireOp",EDGE,"E1.top");var subQ9=sQuery(id+"F0.wireOp",EDGE,"E1.left");var subQ10=sQuery(id+"F0.wireOp",EDGE,"E23.filletArc");var subQ11=sQuery(id+"F0.wireOp",EDGE,"E24.filletArc");Q0=makeQuery(id+"F2.boolean.opBoolean","SPLIT",FACE,{"disambiguationData":[TD([makeQuery(id+"F1.opExtrude","SWEPT_FACE",FACE,{"disambiguationData":[OSD([subQ6])]})])],"derivedFrom":makeQuery(id+"F1.opExtrude","CAP_FACE",FACE,{"disambiguationData":[OSD([subQ6,subQ8,subQ9,subQ7,subQ4,subQ3,subQ2,subQ1,subQ0,subQ5,subQ10,subQ11])],"isStart":true})});}
            var sketch = newSketch(context, id + "F16", { "sketchPlane" : qUnion([Q0])});
            skPoint(sketch, "E79.endSnap0", {"position": v(0, 74.25) * mm});
            skLineSegment(sketch, "E80", {"start": v(0, 60) * mm, "end": v(0, 104.25) * mm, "construction": true});
            skPoint(sketch, "E80.endSnap0", {"position": v(0, 60) * mm});
            skCircle(sketch, "E81", {"center": v(0, 104.25) * mm, "radius": 6 * mm});
            skArc(sketch, "E82", {"start": v(15, 104.25) * mm, "mid": v(0, 119.25) * mm, "end": v(-15, 104.25) * mm});
            skLineSegment(sketch, "E83", {"start": v(-15, 104.25) * mm, "end": v(-15, 92.25) * mm});
            skLineSegment(sketch, "E84", {"start": v(-15, 92.25) * mm, "end": v(-33, 74.25) * mm});
            skLineSegment(sketch, "E85", {"start": v(15, 104.25) * mm, "end": v(15, 92.25) * mm});
            skLineSegment(sketch, "E86", {"start": v(15, 92.25) * mm, "end": v(33, 74.25) * mm});
            skLineSegment(sketch, "E87", {"start": v(32.03, 104.25) * mm, "end": v(-44.62, 104.25) * mm, "construction": true});
            skPoint(sketch, "E88.end.orphan", {"position": v(15, 74.25) * mm});
            skLineSegment(sketch, "E89", {"start": v(-74.25, 0) * mm, "end": v(74.25, 0) * mm, "construction": true});
            skLineSegment(sketch, "E90", {"start": v(0, 60) * mm, "end": v(0, -74.25) * mm, "construction": true});
            skLineSegment(sketch, "E91", {"start": v(0, -74.25) * mm, "end": v(0, -86.75) * mm, "construction": true});
            skPoint(sketch, "E92.MirrorP", {"position": v(15, -222.75) * mm});
            skPoint(sketch, "E93.MirrorP", {"position": v(0, -222.75) * mm});
            skPoint(sketch, "E94.MirrorP", {"position": v(0, -208.5) * mm});
            skLineSegment(sketch, "E95.MirrorCS", {"start": v(0, -208.5) * mm, "end": v(0, -252.75) * mm, "construction": true});
            skLineSegment(sketch, "E96.MirrorCS", {"start": v(32.03, -252.75) * mm, "end": v(-44.62, -252.75) * mm, "construction": true});
            skLineSegment(sketch, "E97.MirrorCS", {"start": v(15, -252.75) * mm, "end": v(15, -240.75) * mm});
            skLineSegment(sketch, "E98.MirrorCS", {"start": v(-15, -240.75) * mm, "end": v(-33, -222.75) * mm});
            skArc(sketch, "E99.MirrorCS", {"start": v(15, -252.75) * mm, "mid": v(0, -267.75) * mm, "end": v(-15, -252.75) * mm});
            skLineSegment(sketch, "E100.MirrorCS", {"start": v(15, -240.75) * mm, "end": v(33, -222.75) * mm});
            skLineSegment(sketch, "E101.MirrorCS", {"start": v(-15, -252.75) * mm, "end": v(-15, -240.75) * mm});
            skCircle(sketch, "E102.MirrorC", {"center": v(0, -252.75) * mm, "radius": 6 * mm});
            skLineSegment(sketch, "E103.MirrorCS", {"start": v(32.03, -104.25) * mm, "end": v(-44.62, -104.25) * mm, "construction": true});
            skLineSegment(sketch, "E104.MirrorCS", {"start": v(15, -92.25) * mm, "end": v(33, -74.25) * mm});
            skLineSegment(sketch, "E105.MirrorCS", {"start": v(15, -104.25) * mm, "end": v(15, -92.25) * mm});
            skLineSegment(sketch, "E106.MirrorCS", {"start": v(-15, -92.25) * mm, "end": v(-33, -74.25) * mm});
            skLineSegment(sketch, "E107.MirrorCS", {"start": v(-15, -104.25) * mm, "end": v(-15, -92.25) * mm});
            skArc(sketch, "E108.MirrorCS", {"start": v(15, -104.25) * mm, "mid": v(0, -119.25) * mm, "end": v(-15, -104.25) * mm});
            skPoint(sketch, "E109.MirrorP", {"position": v(0, -60) * mm});
            skLineSegment(sketch, "E110.MirrorCS", {"start": v(0, -60) * mm, "end": v(0, -104.25) * mm, "construction": true});
            skCircle(sketch, "E111.MirrorC", {"center": v(0, -104.25) * mm, "radius": 6 * mm});
            skPoint(sketch, "E112.MirrorP", {"position": v(15, -74.25) * mm});
            skPoint(sketch, "E113.MirrorP", {"position": v(0, -74.25) * mm});
            skSolve(sketch);
        }
        {
            var Q0;
            Q0=makeQuery(id+"F16.imprint","IMPRINT",FACE,{"disambiguationData":[TD([[makeQuery(id+"F16.imprint","IMPRINT",EDGE,{"derivedFrom":sQuery(id+"F16.wireOp",EDGE,"E81")}),-1.0]])]});
            var Q1;
            {var subQ1=sQuery(id+"F16.wireOp",EDGE,"E104.MirrorCS");Q1=makeQuery(id+"F16.imprint","IMPRINT",FACE,{"disambiguationData":[TD([[makeQuery(id+"F16.imprint","IMPRINT",EDGE,{"derivedFrom":subQ1}),1.0]])]});}
            var Q2;
            Q2=makeQuery(id+"F2.opExtrude","CAP_FACE",FACE,{"disambiguationData":[OSD([sQuery(id+"F0.wireOp",EDGE,"E12"),sQuery(id+"F0.wireOp",EDGE,"E13"),sQuery(id+"F0.wireOp",EDGE,"E14"),sQuery(id+"F0.wireOp",EDGE,"E15"),sQuery(id+"F0.wireOp",EDGE,"E17.filletArc"),sQuery(id+"F0.wireOp",EDGE,"E18.filletArc"),sQuery(id+"F0.wireOp",EDGE,"E19.filletArc"),sQuery(id+"F0.wireOp",EDGE,"E20.filletArc"),sQuery(id+"F0.wireOp",EDGE,"E25.0"),sQuery(id+"F0.wireOp",EDGE,"E25.1"),sQuery(id+"F0.wireOp",EDGE,"E25.2"),sQuery(id+"F0.wireOp",EDGE,"E25.3"),sQuery(id+"F0.wireOp",EDGE,"E25.4"),sQuery(id+"F0.wireOp",EDGE,"E25.5"),sQuery(id+"F0.wireOp",EDGE,"E25.6"),sQuery(id+"F0.wireOp",EDGE,"E25.7")])],"isStart":false});
            extrude(context, id + "F17", {"entities" : qUnion([Q0, Q1]), "endBound" : BoundingType.UP_TO_SURFACE, "depth" : 25 * mm, "endBoundEntityFace" : qUnion([Q2]), "offsetDistance" : 25 * mm});
        }
    });
